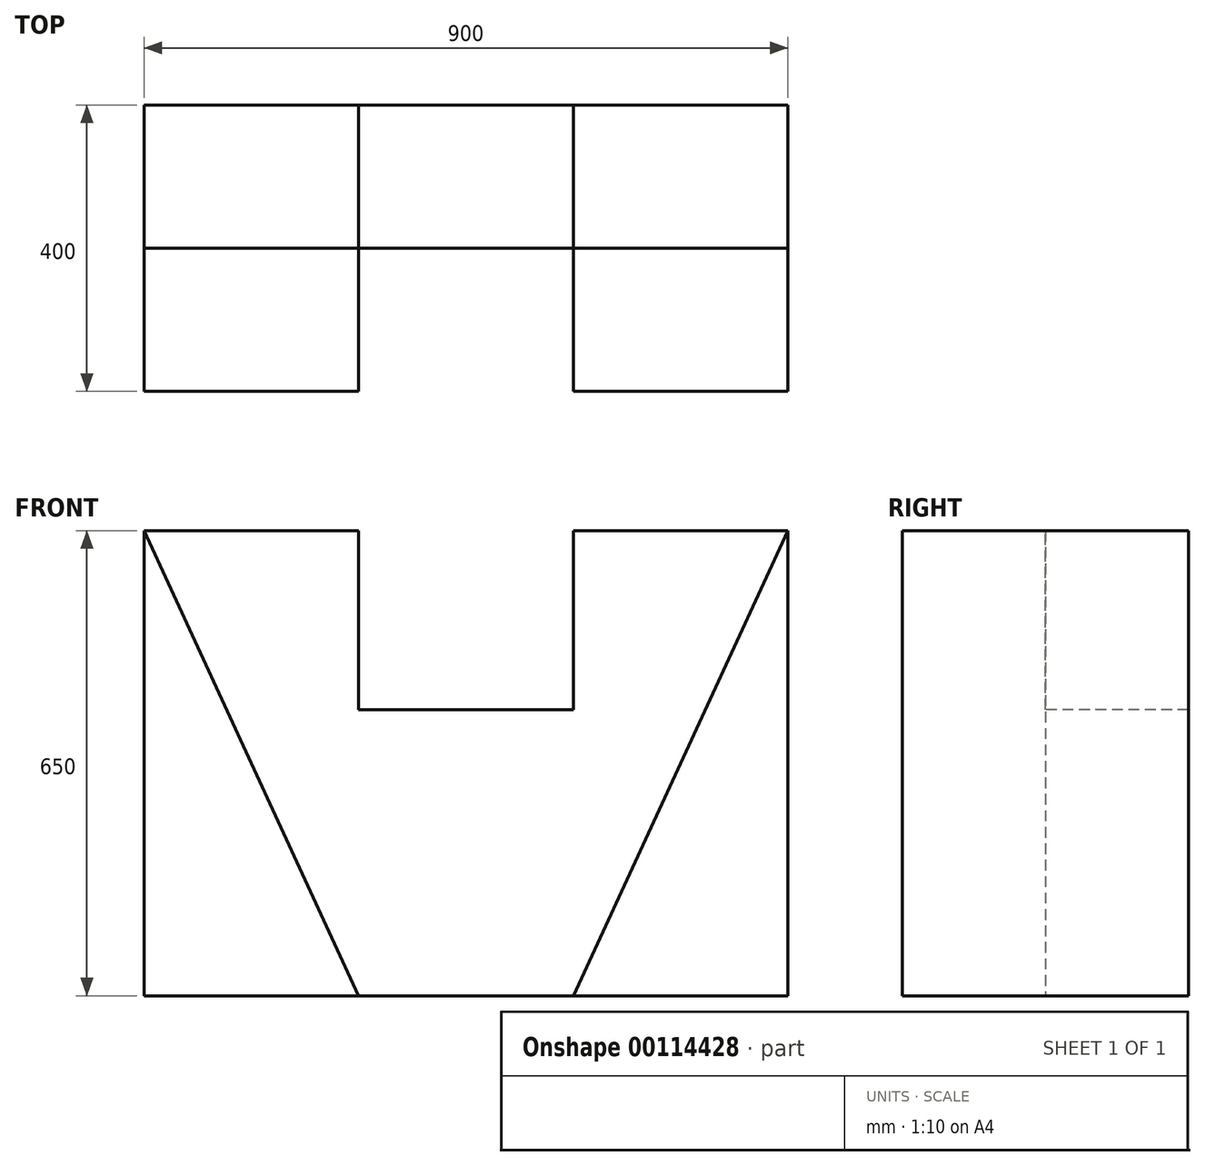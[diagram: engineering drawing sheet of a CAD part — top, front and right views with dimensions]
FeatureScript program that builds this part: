
annotation { "Feature Type Name" : "Feature", "Feature Type Description" : "" }
export const myFeature = defineFeature(function(context is Context, id is Id, definition is map)
    precondition{}
    {
        {
            var Q0;
            Q0=qCreatedBy(makeId("Front.planeOp"),FACE);
            var sketch = newSketch(context, id + "F0", { "sketchPlane" : qUnion([Q0])});
            skLineSegment(sketch, "E0.bottom", {"start": v(450, 325) * mm, "end": v(-450, 325) * mm});
            skLineSegment(sketch, "E0.top", {"start": v(450, -325) * mm, "end": v(-450, -325) * mm});
            skLineSegment(sketch, "E0.left", {"start": v(450, 325) * mm, "end": v(450, -325) * mm});
            skLineSegment(sketch, "E0.right", {"start": v(-450, 325) * mm, "end": v(-450, -325) * mm});
            skPoint(sketch, "E0.middle", {"position": v(0, 0) * mm});
            skSolve(sketch);
        }
        {
            var Q0;
            Q0 = qSketchRegion(id + "F0", true);
            extrude(context, id + "F1", {"entities" : qUnion([Q0]), "depth" : 200 * mm});
        }
        {
            var Q0;
            Q0=makeQuery(id+"F1.opExtrude","CAP_FACE",FACE,{"disambiguationData":[OSD([sQuery(id+"F0.wireOp",EDGE,"E0.bottom"),sQuery(id+"F0.wireOp",EDGE,"E0.top"),sQuery(id+"F0.wireOp",EDGE,"E0.left"),sQuery(id+"F0.wireOp",EDGE,"E0.right")])],"isStart":false});
            var sketch = newSketch(context, id + "F2", { "sketchPlane" : qUnion([Q0])});
            skLineSegment(sketch, "E1", {"start": v(-450, -325) * mm, "end": v(-450, 325) * mm});
            skLineSegment(sketch, "E2", {"start": v(-450, 325) * mm, "end": v(-150, -325) * mm});
            skLineSegment(sketch, "E3", {"start": v(-150, -325) * mm, "end": v(-450, -325) * mm});
            skLineSegment(sketch, "E4", {"start": v(450, -325) * mm, "end": v(450, 325) * mm});
            skLineSegment(sketch, "E5", {"start": v(450, 325) * mm, "end": v(150, -325) * mm});
            skLineSegment(sketch, "E6", {"start": v(150, -325) * mm, "end": v(450, -325) * mm});
            skSolve(sketch);
        }
        {
            var Q0;
            Q0=makeQuery(id+"F2.imprint","IMPRINT",FACE,{"disambiguationData":[TD([[makeQuery(id+"F2.imprint","IMPRINT",EDGE,{"derivedFrom":sQuery(id+"F2.wireOp",EDGE,"E1")}),1.0]])]});
            var Q1;
            Q1=makeQuery(id+"F2.imprint","IMPRINT",FACE,{"disambiguationData":[TD([[makeQuery(id+"F2.imprint","IMPRINT",EDGE,{"derivedFrom":sQuery(id+"F2.wireOp",EDGE,"E1")}),1.0]])]});
            var Q2;
            Q2=makeQuery(id+"F2.imprint","IMPRINT",FACE,{"disambiguationData":[TD([[makeQuery(id+"F2.imprint","IMPRINT",EDGE,{"derivedFrom":sQuery(id+"F2.wireOp",EDGE,"E4")}),-1.0]])]});
            extrude(context, id + "F3", {"entities" : qUnion([Q0, Q1, Q2]), "operationType" : NewBodyOperationType.ADD, "depth" : 200 * mm});
        }
        {
            var Q0;
            Q0=makeQuery(id+"F1.opExtrude","SWEPT_FACE",FACE,{"disambiguationData":[OSD([sQuery(id+"F0.wireOp",EDGE,"E0.bottom")])]});
            var sketch = newSketch(context, id + "F4", { "sketchPlane" : qUnion([Q0])});
            skLineSegment(sketch, "E7.bottom", {"start": v(-150, 0) * mm, "end": v(150, 0) * mm});
            skLineSegment(sketch, "E7.top", {"start": v(-150, -200) * mm, "end": v(150, -200) * mm});
            skLineSegment(sketch, "E7.left", {"start": v(-150, 0) * mm, "end": v(-150, -200) * mm});
            skLineSegment(sketch, "E7.right", {"start": v(150, 0) * mm, "end": v(150, -200) * mm});
            skSolve(sketch);
        }
        {
            var Q0;
            Q0=makeQuery(id+"F4.imprint","IMPRINT",FACE,{"disambiguationData":[TD([[makeQuery(id+"F4.imprint","IMPRINT",EDGE,{"derivedFrom":sQuery(id+"F4.wireOp",EDGE,"E7.bottom")}),1.0]])]});
            extrude(context, id + "F5", {"entities" : qUnion([Q0]), "operationType" : NewBodyOperationType.REMOVE, "oppositeDirection" : true, "depth" : 250 * mm});
        }
    });
